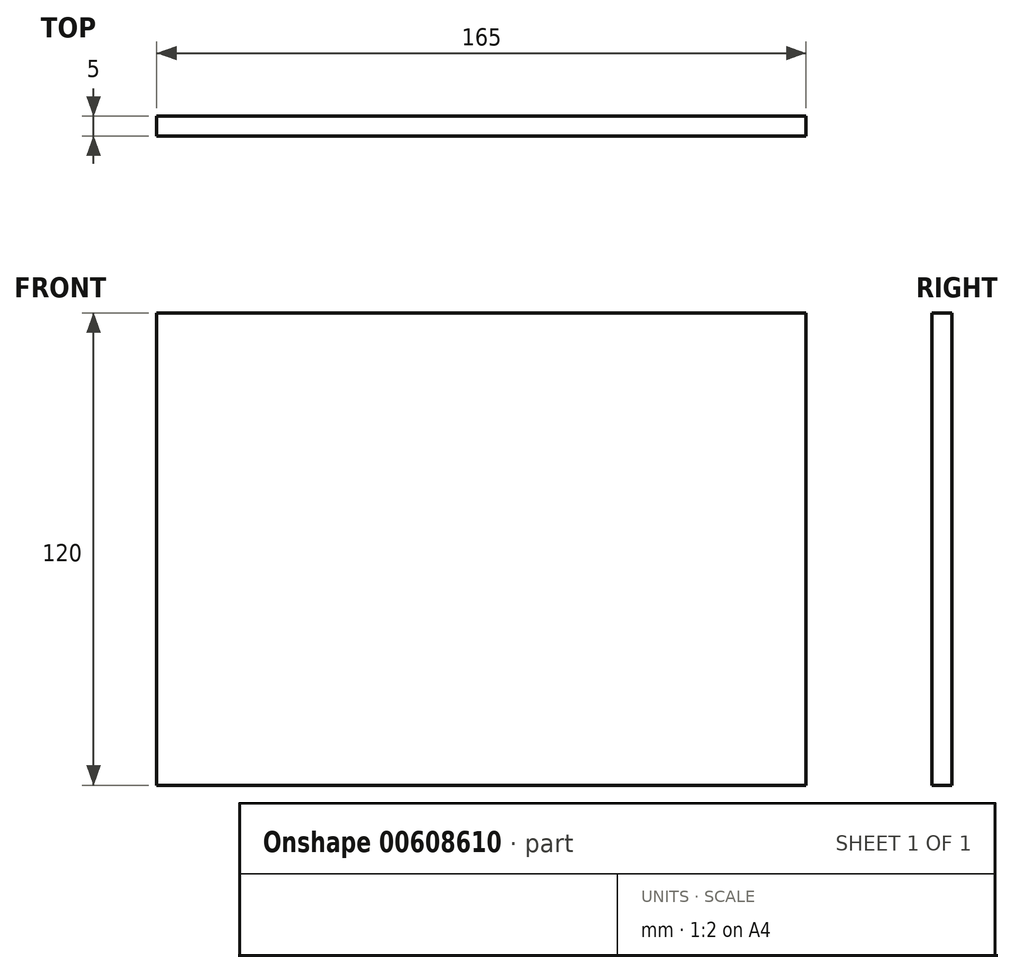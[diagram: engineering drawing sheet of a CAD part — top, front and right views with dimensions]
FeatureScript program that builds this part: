
annotation { "Feature Type Name" : "Feature", "Feature Type Description" : "" }
export const myFeature = defineFeature(function(context is Context, id is Id, definition is map)
    precondition{}
    {
        {
            var Q0;
            Q0=qCreatedBy(makeId("Front.planeOp"),FACE);
            var sketch = newSketch(context, id + "F0", { "sketchPlane" : qUnion([Q0])});
            skLineSegment(sketch, "E0.bottom", {"start": v(0, 0) * mm, "end": v(165, 0) * mm});
            skLineSegment(sketch, "E0.top", {"start": v(0, 120) * mm, "end": v(165, 120) * mm});
            skLineSegment(sketch, "E0.left", {"start": v(0, 0) * mm, "end": v(0, 120) * mm});
            skLineSegment(sketch, "E0.right", {"start": v(165, 0) * mm, "end": v(165, 120) * mm});
            skSolve(sketch);
        }
        {
            var Q0;
            Q0=makeQuery(id+"F0.imprint","IMPRINT",FACE,{"disambiguationData":[TD([[makeQuery(id+"F0.imprint","IMPRINT",EDGE,{"derivedFrom":sQuery(id+"F0.wireOp",EDGE,"E0.bottom")}),1.0]])]});
            extrude(context, id + "F1", {"entities" : qUnion([Q0]), "depth" : 5 * mm, "offsetDistance" : 25 * mm});
        }
    });
